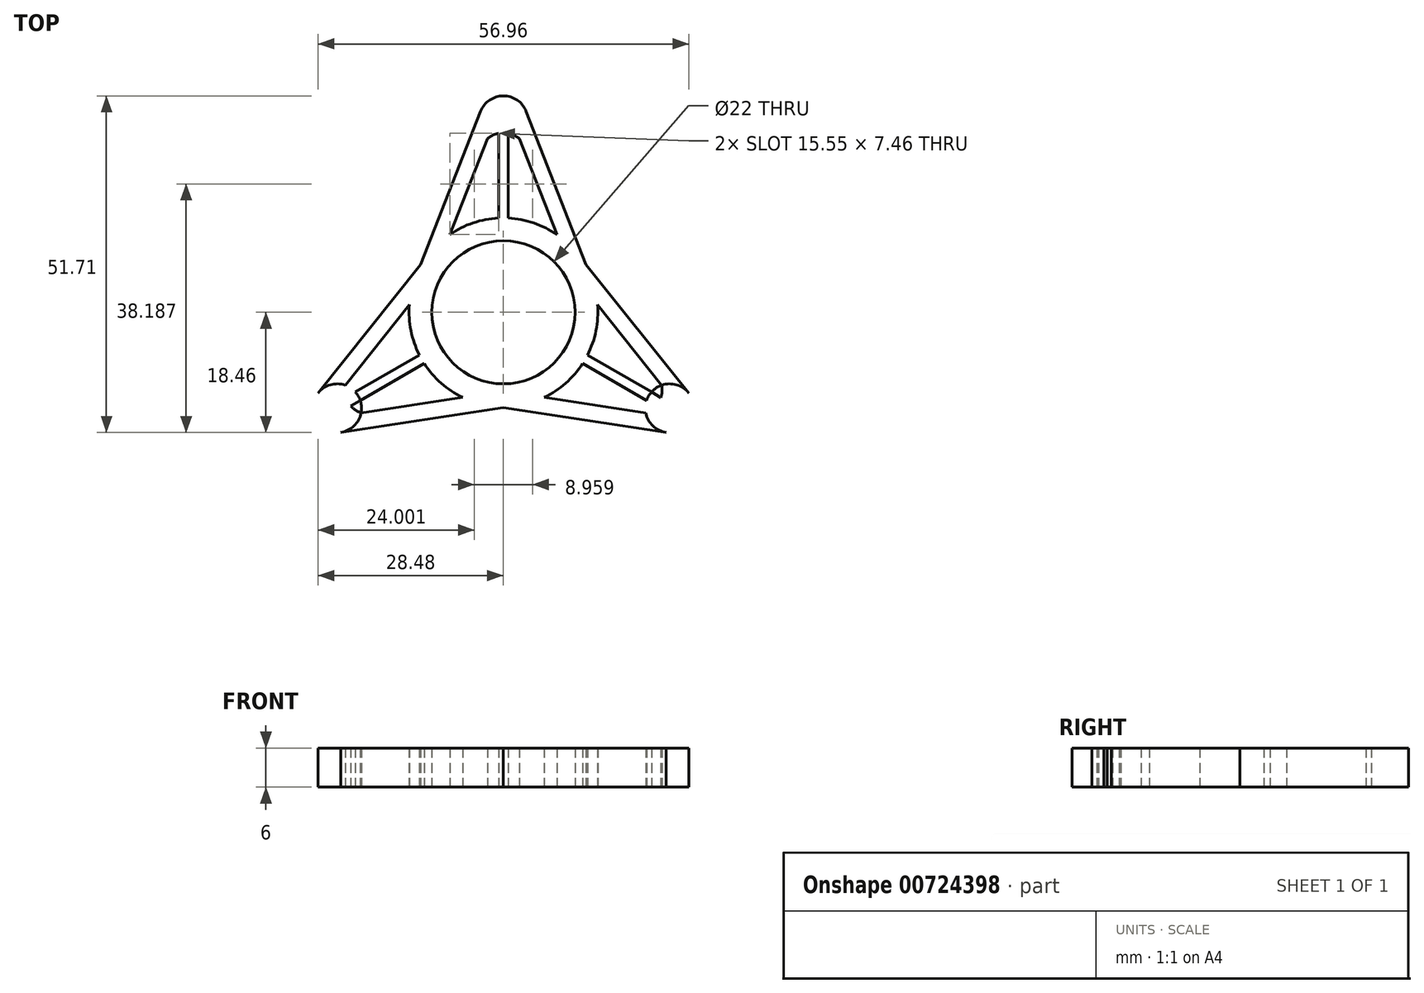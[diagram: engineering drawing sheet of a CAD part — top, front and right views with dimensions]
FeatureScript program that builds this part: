
annotation { "Feature Type Name" : "Feature", "Feature Type Description" : "" }
export const myFeature = defineFeature(function(context is Context, id is Id, definition is map)
    precondition{}
    {
        {
            var Q0;
            Q0=qCreatedBy(makeId("Top.planeOp"),FACE);
            var sketch = newSketch(context, id + "F0", { "sketchPlane" : qUnion([Q0])});
            skCircle(sketch, "E0", {"center": v(0, 0) * mm, "radius": 11 * mm});
            skArc(sketch, "E1", {"start": v(-12.17, -7.89) * mm, "mid": v(-9.57, -10.9) * mm, "end": v(-6.25, -13.09) * mm});
            skLineSegment(sketch, "E2", {"start": v(0, 40.81) * mm, "end": v(0, -43.66) * mm, "construction": true});
            skLineSegment(sketch, "E3", {"start": v(54.3, -31.35) * mm, "end": v(-41.87, 24.17) * mm, "construction": true});
            skLineSegment(sketch, "E4", {"start": v(-54.3, -31.35) * mm, "end": v(45.05, 26.01) * mm, "construction": true});
            skArc(sketch, "E5", {"start": v(3.5, 30.87) * mm, "mid": v(0, 33.25) * mm, "end": v(-3.5, 30.87) * mm});
            skCircle(sketch, "E6.1.0", {"center": v(-25.55, -14.75) * mm, "radius": 3.75 * mm});
            skCircle(sketch, "E6.2.0", {"center": v(25.55, -14.75) * mm, "radius": 3.75 * mm});
            skPoint(sketch, "E7", {"position": v(0, 33.25) * mm});
            skLineSegment(sketch, "E8", {"start": v(3.5, 30.87) * mm, "end": v(12.7, 7.33) * mm});
            skLineSegment(sketch, "E9", {"start": v(2.45, 26.66) * mm, "end": v(8.2, 11.95) * mm});
            skArc(sketch, "E10", {"start": v(2.45, 26.66) * mm, "mid": v(1.66, 27.2) * mm, "end": v(0.75, 27.5) * mm});
            skLineSegment(sketch, "E11.MirrorCS", {"start": v(-2.45, 26.66) * mm, "end": v(-8.2, 11.95) * mm});
            skLineSegment(sketch, "E12.MirrorCS", {"start": v(-3.5, 30.87) * mm, "end": v(-12.7, 7.33) * mm});
            skLineSegment(sketch, "E13.MirrorCS", {"start": v(28.48, -12.4) * mm, "end": v(12.7, 7.33) * mm});
            skLineSegment(sketch, "E14.MirrorCS", {"start": v(24.32, -11.2) * mm, "end": v(14.46, 1.13) * mm});
            skLineSegment(sketch, "E15.MirrorCS", {"start": v(-28.48, -12.4) * mm, "end": v(-12.7, 7.33) * mm});
            skLineSegment(sketch, "E16.MirrorCS", {"start": v(-24.32, -11.2) * mm, "end": v(-14.46, 1.13) * mm});
            skLineSegment(sketch, "E17.MirrorCS", {"start": v(-21.86, -15.46) * mm, "end": v(-6.25, -13.09) * mm});
            skLineSegment(sketch, "E18.MirrorCS", {"start": v(-24.99, -18.46) * mm, "end": v(0, -14.67) * mm});
            skLineSegment(sketch, "E19.MirrorCS", {"start": v(21.86, -15.46) * mm, "end": v(6.25, -13.09) * mm});
            skLineSegment(sketch, "E20.MirrorCS", {"start": v(24.99, -18.46) * mm, "end": v(0, -14.67) * mm});
            skArc(sketch, "E21.trimOffspring", {"start": v(-3.73, 23.4) * mm, "mid": v(0, 20.08) * mm, "end": v(3.73, 23.4) * mm, "construction": true});
            skArc(sketch, "E22.trimOffspring", {"start": v(-2.45, 26.66) * mm, "mid": v(0, 25.75) * mm, "end": v(2.45, 26.66) * mm, "construction": true});
            skArc(sketch, "E23.MirrorCS", {"start": v(-21.86, -15.46) * mm, "mid": v(-22.72, -15.03) * mm, "end": v(-23.44, -14.4) * mm});
            skArc(sketch, "E24.MirrorCS", {"start": v(-22.13, -8.48) * mm, "mid": v(-17.39, -10.04) * mm, "end": v(-18.4, -14.93) * mm, "construction": true});
            skArc(sketch, "E25.MirrorCS", {"start": v(24.32, -11.2) * mm, "mid": v(24.38, -12.16) * mm, "end": v(24.2, -13.1) * mm});
            skArc(sketch, "E26.MirrorCS", {"start": v(18.4, -14.93) * mm, "mid": v(17.39, -10.04) * mm, "end": v(22.13, -8.48) * mm, "construction": true});
            skLineSegment(sketch, "E27", {"start": v(-0.75, 27.5) * mm, "end": v(-0.75, 14.48) * mm});
            skLineSegment(sketch, "E28.MirrorCS", {"start": v(0.75, 27.5) * mm, "end": v(0.75, 14.48) * mm});
            skLineSegment(sketch, "E29.MirrorCS", {"start": v(24.2, -13.1) * mm, "end": v(12.92, -6.6) * mm});
            skLineSegment(sketch, "E30.MirrorCS", {"start": v(23.44, -14.4) * mm, "end": v(12.17, -7.89) * mm});
            skLineSegment(sketch, "E31.MirrorCS", {"start": v(-24.2, -13.1) * mm, "end": v(-12.92, -6.6) * mm});
            skLineSegment(sketch, "E32.MirrorCS", {"start": v(-23.44, -14.4) * mm, "end": v(-12.17, -7.89) * mm});
            skArc(sketch, "E33.trimOffspring", {"start": v(-24.2, -13.1) * mm, "mid": v(-24.38, -12.16) * mm, "end": v(-24.32, -11.2) * mm});
            skArc(sketch, "E34.trimOffspring", {"start": v(23.44, -14.4) * mm, "mid": v(22.72, -15.03) * mm, "end": v(21.86, -15.46) * mm});
            skArc(sketch, "E35.trimOffspring", {"start": v(12.92, -6.6) * mm, "mid": v(14.22, -2.84) * mm, "end": v(14.46, 1.13) * mm});
            skArc(sketch, "E36.trimOffspring", {"start": v(-0.75, 14.48) * mm, "mid": v(-4.65, 13.73) * mm, "end": v(-8.2, 11.95) * mm});
            skArc(sketch, "E37.trimOffspring", {"start": v(-0.75, 27.5) * mm, "mid": v(-1.66, 27.2) * mm, "end": v(-2.45, 26.66) * mm});
            skArc(sketch, "E38.trimOffspring", {"start": v(-14.46, 1.13) * mm, "mid": v(-14.2, -2.83) * mm, "end": v(-12.92, -6.6) * mm});
            skPoint(sketch, "E39.orphan", {"position": v(-11.33, 9.05) * mm});
            skPoint(sketch, "E40.orphan", {"position": v(-13.5, 5.28) * mm});
            skArc(sketch, "E41.trimOffspring", {"start": v(6.25, -13.09) * mm, "mid": v(9.57, -10.9) * mm, "end": v(12.17, -7.89) * mm});
            skPoint(sketch, "E42.orphan", {"position": v(2.18, -14.34) * mm});
            skPoint(sketch, "E43.orphan", {"position": v(-2.18, -14.34) * mm});
            skArc(sketch, "E44.trimOffspring", {"start": v(8.2, 11.95) * mm, "mid": v(4.65, 13.71) * mm, "end": v(0.75, 14.48) * mm});
            skPoint(sketch, "E45.orphan", {"position": v(11.33, 9.05) * mm});
            skPoint(sketch, "E46.orphan", {"position": v(13.5, 5.28) * mm});
            skSolve(sketch);
        }
        {
            var Q0;
            {var subQ5=sQuery(id+"F0.wireOp",EDGE,"E23.MirrorCS");Q0=makeQuery(id+"F0.imprint","IMPRINT",FACE,{"disambiguationData":[TD([[makeQuery(id+"F0.imprint","IMPRINT",EDGE,{"derivedFrom":subQ5}),1.0]])]});}
            var Q1;
            Q1=makeQuery(id+"F0.imprint","IMPRINT",FACE,{"disambiguationData":[TD([[makeQuery(id+"F0.imprint","IMPRINT",EDGE,{"derivedFrom":sQuery(id+"F0.wireOp",EDGE,"E0")}),-1.0]])]});
            var Q2;
            {var subQ7=sQuery(id+"F0.wireOp",EDGE,"E25.MirrorCS");Q2=makeQuery(id+"F0.imprint","IMPRINT",FACE,{"disambiguationData":[TD([[makeQuery(id+"F0.imprint","IMPRINT",EDGE,{"derivedFrom":subQ7}),1.0]])]});}
            extrude(context, id + "F1", {"entities" : qUnion([Q0, Q1, Q2]), "depth" : 6 * mm, "offsetDistance" : 25 * mm});
        }
    });
